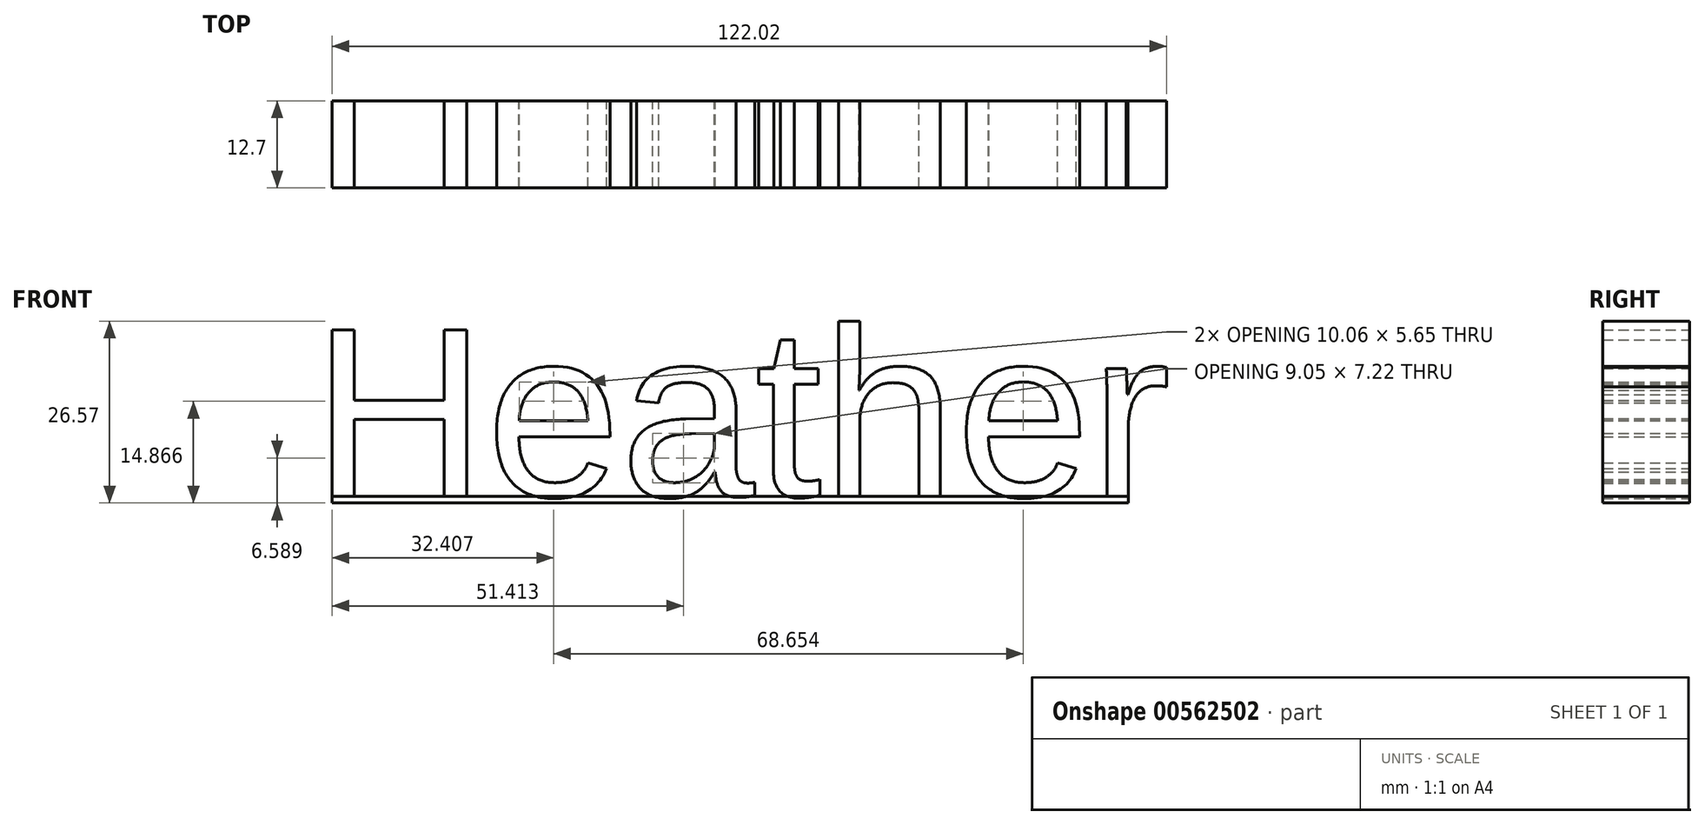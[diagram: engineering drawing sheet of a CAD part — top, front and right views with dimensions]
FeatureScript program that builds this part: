
annotation { "Feature Type Name" : "Feature", "Feature Type Description" : "" }
export const myFeature = defineFeature(function(context is Context, id is Id, definition is map)
    precondition{}
    {
        {
            var Q0;
            Q0=qCreatedBy(makeId("Front.planeOp"),FACE);
            var sketch = newSketch(context, id + "F0", { "sketchPlane" : qUnion([Q0])});
            skText(sketch, "E0", { "text": "Heather", "fontName": "Arimo-Regular.ttf"});
            skPoint(sketch, "E1", {"position": v(0, 12.7) * mm});
            const initialGuessF0  = {"E0": [-0.06368, 0, 1, 0, 0.0254]};
            skSetInitialGuess(sketch, initialGuessF0);
            skSolve(sketch);
        }
        {
            var Q0;
            Q0=qSketchRegion(id+"F0",true);
            extrude(context, id + "F1", {"entities" : qUnion([Q0]), "endBound" : BoundingType.SYMMETRIC, "depth" : 12.7 * mm, "offsetDistance" : 25.4 * mm});
        }
        {
            var Q0;
            Q0=qCreatedBy(makeId("Top.planeOp"),FACE);
            var sketch = newSketch(context, id + "F2", { "sketchPlane" : qUnion([Q0])});
            skPoint(sketch, "E2.0", {"position": v(-60.79, 0) * mm});
            skLineSegment(sketch, "E3.0", {"start": v(-60.79, -6.35) * mm, "end": v(-60.79, 6.35) * mm});
            skLineSegment(sketch, "E4.0", {"start": v(55.61, -6.35) * mm, "end": v(55.61, 6.35) * mm});
            skLineSegment(sketch, "E5", {"start": v(-60.79, -6.35) * mm, "end": v(55.61, -6.35) * mm});
            skLineSegment(sketch, "E6", {"start": v(55.61, 6.35) * mm, "end": v(-60.79, 6.35) * mm});
            skSolve(sketch);
        }
        {
            var Q0;
            Q0=makeQuery(id+"F2.imprint","IMPRINT",FACE,{"disambiguationData":[TD([[makeQuery(id+"F2.imprint","IMPRINT",EDGE,{"derivedFrom":sQuery(id+"F2.wireOp",EDGE,"E3.0")}),-1.0]])]});
            extrude(context, id + "F3", {"entities" : qUnion([Q0]), "oppositeDirection" : true, "depth" : 1 * mm, "offsetDistance" : 25.4 * mm});
        }
    });
